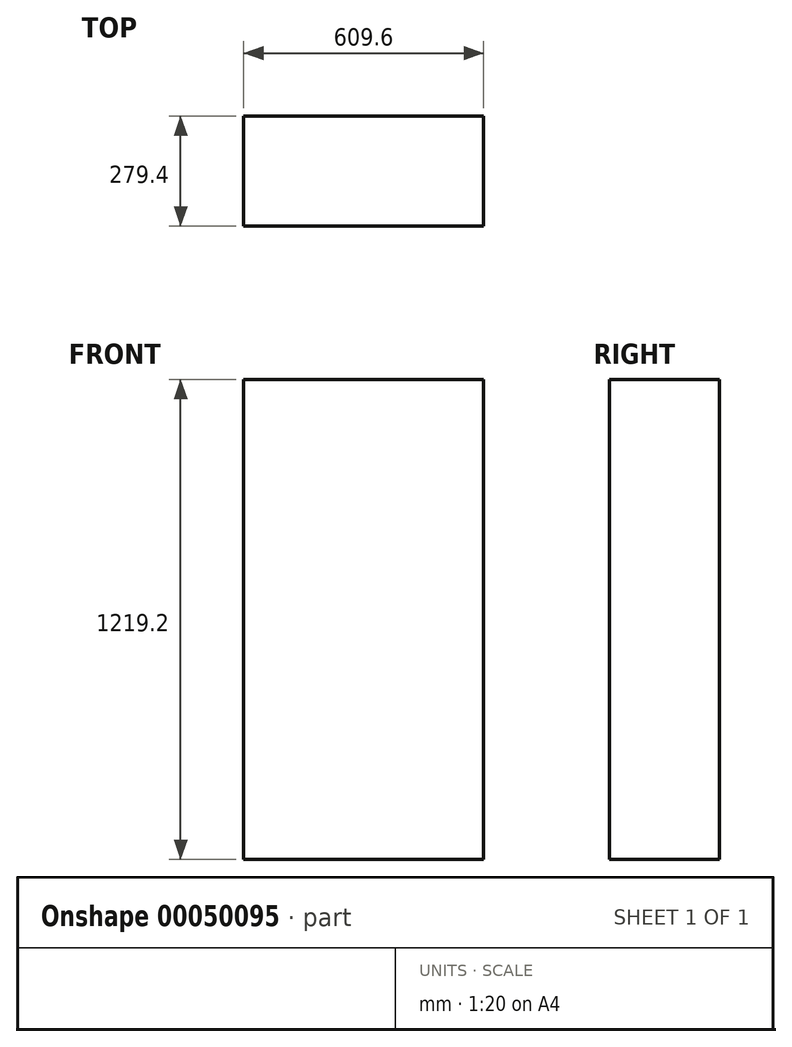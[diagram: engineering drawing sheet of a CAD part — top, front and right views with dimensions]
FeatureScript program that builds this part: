
annotation { "Feature Type Name" : "Feature", "Feature Type Description" : "" }
export const myFeature = defineFeature(function(context is Context, id is Id, definition is map)
    precondition{}
    {
        {
            var Q0;
            Q0=qCreatedBy(makeId("Top.planeOp"),FACE);
            var sketch = newSketch(context, id + "F0", { "sketchPlane" : qUnion([Q0])});
            skLineSegment(sketch, "E0.bottom", {"start": v(-304.8, -139.7) * mm, "end": v(304.8, -139.7) * mm});
            skLineSegment(sketch, "E0.top", {"start": v(-304.8, 139.7) * mm, "end": v(304.8, 139.7) * mm});
            skLineSegment(sketch, "E0.left", {"start": v(-304.8, -139.7) * mm, "end": v(-304.8, 139.7) * mm});
            skLineSegment(sketch, "E0.right", {"start": v(304.8, -139.7) * mm, "end": v(304.8, 139.7) * mm});
            skSolve(sketch);
        }
        {
            var Q0;
            Q0 = qSketchRegion(id + "F0", true);
            extrude(context, id + "F1", {"entities" : qUnion([Q0]), "depth" : 1219.2 * mm});
        }
    });
